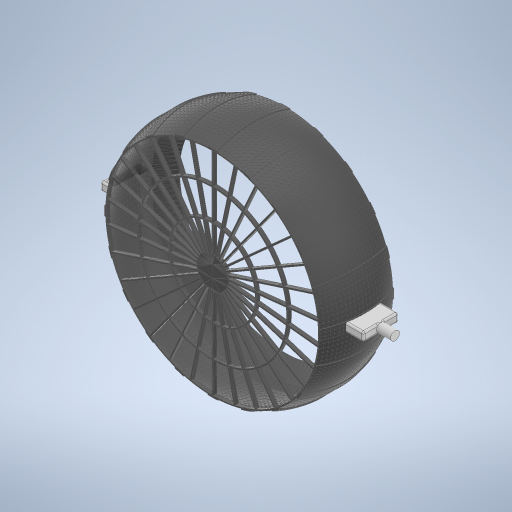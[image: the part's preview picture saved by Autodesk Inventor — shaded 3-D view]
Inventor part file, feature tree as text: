
AUTODESK INVENTOR PART (.ipt)
format: ipt  version: 2024 (Build 280153000, 153)  size: 741,376 bytes
history: native  units: mm
features: extrude x5, sketch x5, projected_geometry x4, other x2, plane x2, fillet x2
ambient origin geometry x8: Origin, YZ Plane, XZ Plane, XY Plane, X Axis, Y Axis, Z Axis, Center Point
bodies: Solid1 (feature_tree)
feature tree (20):
  other  "protection_cover_front"
  plane  "Work Plane2"
  plane  "Work Plane3"
  extrude  "Extrusion1"  Depth=5.0mm
  extrude  "Extrusion2"  Depth=10.0mm TaperAngle=0.0deg
  extrude  "Extrusion3"  Depth=1.0mm
  fillet  "Fillet1"  Radius=1.0mm
  extrude  "Extrusion4"  TaperAngle=0.0deg  [1 undecoded]
  extrude  "Extrusion6"  Depth=1.0mm
  fillet  "Fillet2"  Radius=20.0mm
  sketch  "Sketch2"  dims[d1=130.263mm d2=1.086mm d3=5.0mm]
  sketch  "Sketch3"  dims[d4=20.0mm d5=10.0mm d6=0.0mm]
  projected_geometry  "Projected Loop1"
  sketch  "Sketch4"  dims[d7=2.0mm d8=52.0mm d9=1.0mm]
  projected_geometry  "Projected Loop2"
  sketch  "Sketch5"  dims[d10=1.0mm d20=0.0mm d21=0.0mm]
  projected_geometry  "Projected Loop3"
  sketch  "Sketch7"  dims[d29=10.0mm d30=0.0mm d31=1.0mm d32=20.0mm d33=5.0mm d35=10.0mm d36=0.0mm d47=5.0mm d48=8.0mm d49=0.0mm d50=1.0mm d51=2.3mm]
  projected_geometry  "Projected Loop4"
  other  "MeshFeature1"
note: 1 required parameter value undecoded (feature->parameter linkage not recoverable at this tier; creation-order binding heuristic only, values carry confidence <= 0.55)
